# Revit family: Kessel 48003.43M en
name_source: partatom
category: Pipe Accessories
revit_build: Autodesk Revit Architecture 2014 (Build: 20130308_1515(x64)
units: mm (PartAtom-declared; Revit-internal decimal feet)

## types (1)
- Kessel 48003.43M en
    <1.010.00.2> Number of the part of the guideline = 38
    <1.010.00.3> Issue date (month) of the guideline = 201805
    <1.010.00.4> Manufacturer name = Kessel
    <1.010.00.5> Revision date of the file = 20190228
    <1.800.00.3> BS number = 00105000000200100000200000100300000000400100000003???00001
    <1.800.00.4> Comment field = Scada LED wall drain w. Wave drain cov., 1.4301, fixed membrane flange
    <1.810.00.3> Manufacturer’s reference number = 48003.43M
    <1.810.00.4> DATANORM number = 48003.43M
    <1.960/3L.00.8> Link (URL) = http://www.kessel.de
    <38.100.00.4> Drain type for floor, roof and sanitary objects = Floor drains with odour trap
    <38.110.00.4> Floor, roof and sanitary works sequences = Scada LED wall drain
    <38.200.00.3> Drain socket variation = horizontal
    <38.250.00.3> Drainage type = open channel
    <38.300.00.3> Type of drains for floor, roof and roofing objects = linear drain (e.g. channel)
    <38.360.00.3> Trace heating of the drain for floor, roof and sanitary objects = without auxiliary heating
    <38.400.00.3> Material of the drain body = polymer
    <38.500.00.3> Sealing variantion = with factory-mounted membrane
    <38.550.00.3> Trap = with odour trap
    <38.700.00.15> Connection to GLT, GA = no
    <38.700.00.16> Fire resistance class can be retrofitted = no
    <38.700.00.4> product name = Scada LED wall drain w. Wave drain cov., 1.4301, fixed membrane flange
    <38.700.00.6> Complete article (one-piece) from combination (multi-part design) Drain body and attachment piece = yes
    <38.700.00.7> Potential compensation (ground connection) available = no
    <38.700.00.8> Electrical connection = yes
    <38.710.01.10> depth [mm] = 195
    <38.710.01.11> installation height [mm] = 353
    <38.710.01.12> Water trap [mm] = 22
    <38.710.01.14> with sound decoupling = yes
    <38.710.01.15> Leafy / Kiefang = no
    <38.710.01.3> Product name = Scada LED wall drain w. Wave drain cov., 1.4301, fixed membrane flange
    <38.710.01.4> Type = wall drain
    <38.710.01.5> Nominal system = DN
    <38.710.01.6> Nominal dimensions = 50
    <38.710.01.9> installation width [mm] = 362
    <38.710.11.3> drainage capacity [l/s] = 0.5
    <38.710.11.4> Water level difference (accumulation height) [mm] = 20
    <38.710.12.12> Rust included [mm] = yes
    <38.710.12.3> Product name = Scada LED wall drain w. Wave drain cov., 1.4301, fixed membrane flange
    <38.710.12.6> Material of the attachment pieces = plastic
    <38.710.12.7> Shape = rectangular
    <38.710.13.3> Product name = Scada LED wall drain w. Wave drain cov., 1.4301, fixed membrane flange
    <38.710.13.4> Variant of the drainage drain = point drain
    <38.710.13.5> Type gutter = rectangular
    <38.710.13.7> Leafy / Kiefang = no
    <38.710.14.10> Rust included = yes
    <38.710.14.3> Product name = Scada LED wall drain w. Wave drain cov., 1.4301, fixed membrane flange
    <38.710.14.5> Max. installation length [mm] = 312
    <38.710.15.12> Max. installation length [mm] = 312
    <38.710.15.3> Product name = Scada drain cover, stainless steel 1.4301
    <38.710.15.4> Execution drain grate = tileable drain cover
    <38.710.15.5> Material of the drain grate = Stainless steel
    <38.710.15.6> Fixing the grate = clamped
    <38.710.15.7> Execution of the drain grate = tileable drain cover
    <38.710.15.8> Surface drain grate = brushed
    <38.710.15.9> Slip resistance of the drain grate = no
    <38.710.16.3> Type of measurements = external dimensions
    CONNECTOR0_ref_dY = 18 mm
    CONNECTOR0_ref_dZ = 51 mm
    CONNECTOR1_DIAMETER_dX_0r = 0 mm  [stored 0 ft]
    CONNECTOR1_dX_00 = 134 mm
    CONNECTOR1_dX_01 = 124 mm
    CONNECTOR1_ref_dX = 124 mm
    CONNECTOR1_ref_dY = 62 mm
    CONNECTOR1_ref_dZ = 55 mm  [stored 0.180446 ft]
    CONNECTOR2_DIAMETER_dY_0r = 0 mm  [stored 0 ft]
    CONNECTOR2_dY_00 = 83 mm
    CONNECTOR2_dY_01 = 63 mm
    CONNECTOR2_ref_dY = 63 mm
    CONNECTOR2_ref_dZ = 40 mm
    CONNECTOR3_DIAMETER_dX_0r = 0 mm  [stored 0 ft]
    CONNECTOR3_dX_00 = 110 mm
    CONNECTOR3_dX_01 = 90 mm
    CONNECTOR3_ref_dX = 90 mm
    CONNECTOR3_ref_dY = 60 mm
    CONNECTOR3_ref_dZ = 40 mm
    CONNECTOR4_DIAMETER_dX_0r = 0 mm  [stored 0 ft]
    CONNECTOR4_dX_00 = 90 mm
    CONNECTOR4_dX_01 = 110 mm
    CONNECTOR4_ref_dX = 90 mm
    CONNECTOR4_ref_dY = 60 mm
    CONNECTOR4_ref_dZ = 40 mm
    Manufacturer = Kessel
    Model = 48003.43M
    URL = www.kessel.com

note: [stored X ft] marks values corroborated as IEEE doubles in the binary element streams (Revit-internal decimal feet)
